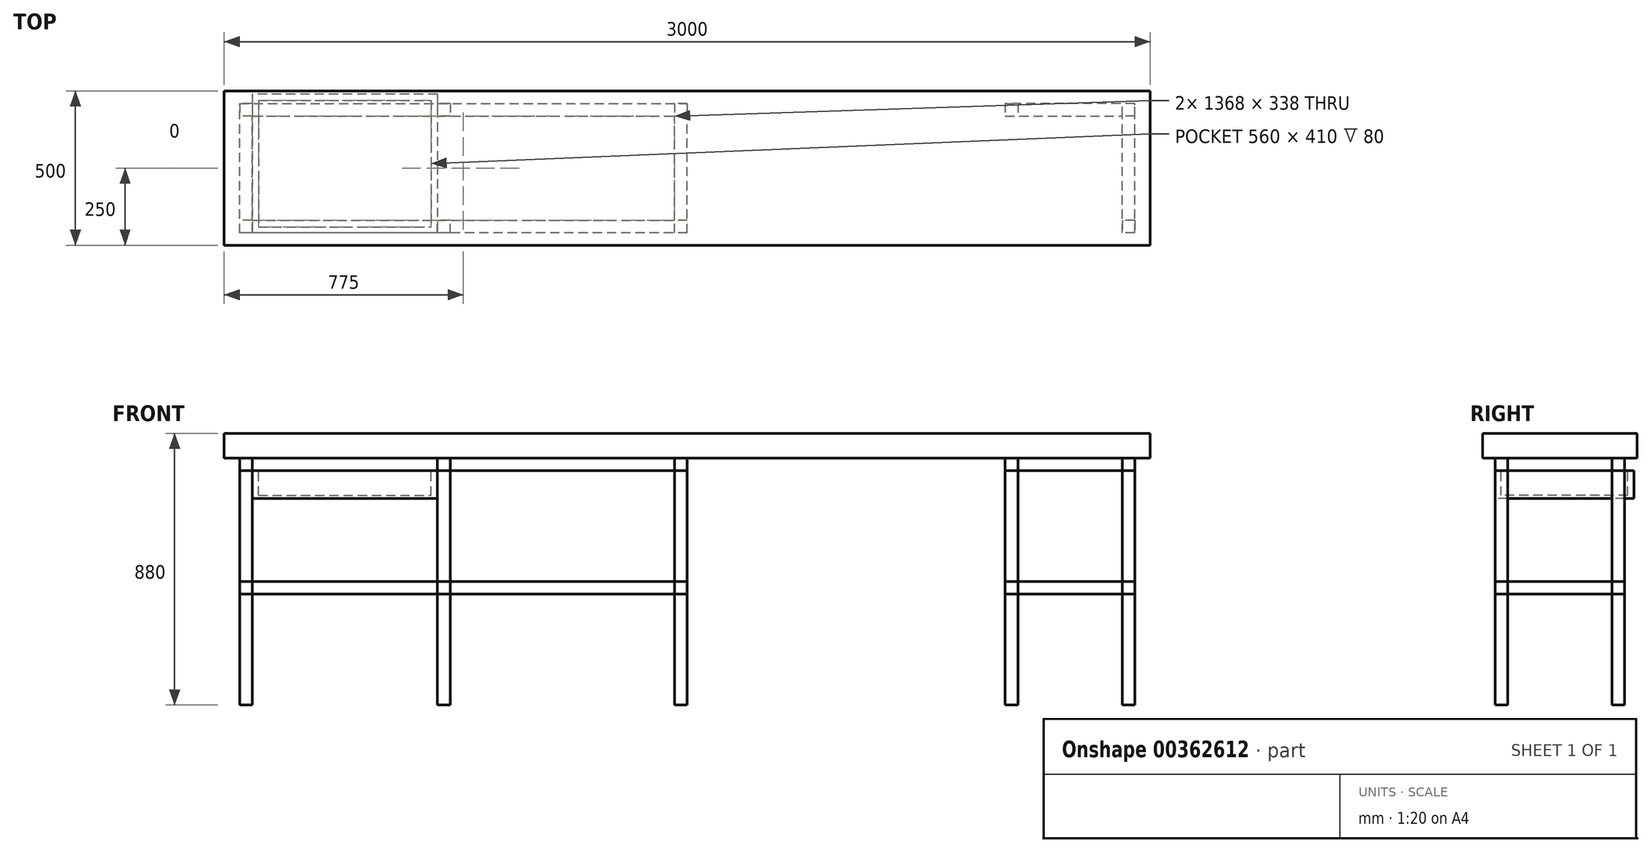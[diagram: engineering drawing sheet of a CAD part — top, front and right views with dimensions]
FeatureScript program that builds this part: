
annotation { "Feature Type Name" : "Feature", "Feature Type Description" : "" }
export const myFeature = defineFeature(function(context is Context, id is Id, definition is map)
    precondition{}
    {
        {
            var Q0;
            Q0=qCreatedBy(makeId("Top.planeOp"),FACE);
            var sketch = newSketch(context, id + "F0", { "sketchPlane" : qUnion([Q0])});
            skLineSegment(sketch, "E0.bottom", {"start": v(0, 0) * mm, "end": v(3000, 0) * mm});
            skLineSegment(sketch, "E0.top", {"start": v(0, 500) * mm, "end": v(3000, 500) * mm});
            skLineSegment(sketch, "E0.left", {"start": v(0, 0) * mm, "end": v(0, 500) * mm});
            skLineSegment(sketch, "E0.right", {"start": v(3000, 0) * mm, "end": v(3000, 500) * mm});
            skSolve(sketch);
        }
        {
            var Q0;
            Q0 = qSketchRegion(id + "F0", true);
            extrude(context, id + "F1", {"entities" : qUnion([Q0]), "depth" : 80 * mm});
        }
        {
            var Q0;
            Q0=makeQuery(id+"F1.opExtrude","CAP_FACE",FACE,{"disambiguationData":[OSD([sQuery(id+"F0.wireOp",EDGE,"E0.bottom"),sQuery(id+"F0.wireOp",EDGE,"E0.top"),sQuery(id+"F0.wireOp",EDGE,"E0.left"),sQuery(id+"F0.wireOp",EDGE,"E0.right")])],"isStart":true});
            var sketch = newSketch(context, id + "F2", { "sketchPlane" : qUnion([Q0])});
            skLineSegment(sketch, "E1.bottom", {"start": v(91, -40) * mm, "end": v(50, -40) * mm});
            skLineSegment(sketch, "E1.top", {"start": v(91, -81) * mm, "end": v(50, -81) * mm});
            skLineSegment(sketch, "E1.left", {"start": v(91, -40) * mm, "end": v(91, -81) * mm});
            skLineSegment(sketch, "E1.right", {"start": v(50, -40) * mm, "end": v(50, -81) * mm});
            skPoint(sketch, "E1.middle", {"position": v(70.5, -60.5) * mm});
            skLineSegment(sketch, "E2.bottom", {"start": v(3000, 0) * mm, "end": v(0, 0) * mm, "construction": true});
            skLineSegment(sketch, "E2.top", {"start": v(3000, -500) * mm, "end": v(0, -500) * mm, "construction": true});
            skLineSegment(sketch, "E2.left", {"start": v(3000, 0) * mm, "end": v(3000, -500) * mm, "construction": true});
            skLineSegment(sketch, "E2.right", {"start": v(0, 0) * mm, "end": v(0, -500) * mm, "construction": true});
            skPoint(sketch, "E2.middle", {"position": v(1500, -250) * mm});
            skLineSegment(sketch, "E3.bottom", {"start": v(2950, -40) * mm, "end": v(50, -40) * mm, "construction": true});
            skLineSegment(sketch, "E3.top", {"start": v(2950, -460) * mm, "end": v(50, -460) * mm, "construction": true});
            skLineSegment(sketch, "E3.left", {"start": v(2950, -40) * mm, "end": v(2950, -460) * mm, "construction": true});
            skLineSegment(sketch, "E3.right", {"start": v(50, -40) * mm, "end": v(50, -460) * mm, "construction": true});
            skLineSegment(sketch, "E4", {"start": v(50, -250) * mm, "end": v(0, -250) * mm, "construction": true});
            skLineSegment(sketch, "E5", {"start": v(1500, -460) * mm, "end": v(1500, -500) * mm, "construction": true});
            skLineSegment(sketch, "E6.bottom", {"start": v(91, -460) * mm, "end": v(50, -460) * mm});
            skLineSegment(sketch, "E6.top", {"start": v(91, -419) * mm, "end": v(50, -419) * mm});
            skLineSegment(sketch, "E6.left", {"start": v(91, -460) * mm, "end": v(91, -419) * mm});
            skLineSegment(sketch, "E6.right", {"start": v(50, -460) * mm, "end": v(50, -419) * mm});
            skPoint(sketch, "E6.middle", {"position": v(70.5, -439.5) * mm});
            skLineSegment(sketch, "E7.right", {"start": v(2812.92, 127.48) * mm, "end": v(2812.92, 114.66) * mm});
            skLineSegment(sketch, "E8.bottom", {"start": v(2950, -81) * mm, "end": v(2909, -81) * mm});
            skLineSegment(sketch, "E8.top", {"start": v(2950, -40) * mm, "end": v(2909, -40) * mm});
            skLineSegment(sketch, "E8.left", {"start": v(2950, -81) * mm, "end": v(2950, -40) * mm});
            skLineSegment(sketch, "E8.right", {"start": v(2909, -81) * mm, "end": v(2909, -40) * mm});
            skPoint(sketch, "E8.middle", {"position": v(2929.5, -60.5) * mm});
            skLineSegment(sketch, "E9.bottom", {"start": v(2950, -419) * mm, "end": v(2909, -419) * mm});
            skLineSegment(sketch, "E9.top", {"start": v(2950, -460) * mm, "end": v(2909, -460) * mm});
            skLineSegment(sketch, "E9.left", {"start": v(2950, -419) * mm, "end": v(2950, -460) * mm});
            skLineSegment(sketch, "E9.right", {"start": v(2909, -419) * mm, "end": v(2909, -460) * mm});
            skPoint(sketch, "E9.middle", {"position": v(2929.5, -439.5) * mm});
            skLineSegment(sketch, "E10.bottom", {"start": v(1500, -460) * mm, "end": v(1459, -460) * mm});
            skLineSegment(sketch, "E10.top", {"start": v(1500, -419) * mm, "end": v(1459, -419) * mm});
            skLineSegment(sketch, "E10.left", {"start": v(1500, -460) * mm, "end": v(1500, -419) * mm});
            skLineSegment(sketch, "E10.right", {"start": v(1459, -460) * mm, "end": v(1459, -419) * mm});
            skPoint(sketch, "E10.middle", {"position": v(1479.5, -439.5) * mm});
            skLineSegment(sketch, "E11", {"start": v(1500, 0) * mm, "end": v(1500, -40) * mm, "construction": true});
            skLineSegment(sketch, "E12.bottom", {"start": v(1500, -40) * mm, "end": v(1459, -40) * mm});
            skLineSegment(sketch, "E12.top", {"start": v(1500, -81) * mm, "end": v(1459, -81) * mm});
            skLineSegment(sketch, "E12.left", {"start": v(1500, -40) * mm, "end": v(1500, -81) * mm});
            skLineSegment(sketch, "E12.right", {"start": v(1459, -40) * mm, "end": v(1459, -81) * mm});
            skPoint(sketch, "E12.middle", {"position": v(1479.5, -60.5) * mm});
            skLineSegment(sketch, "E13", {"start": v(2909, -419) * mm, "end": v(2909, -81) * mm, "construction": true});
            skLineSegment(sketch, "E14", {"start": v(2909, -419) * mm, "end": v(2571, -419) * mm, "construction": true});
            skLineSegment(sketch, "E15.bottom", {"start": v(2530, -460) * mm, "end": v(2571, -460) * mm});
            skLineSegment(sketch, "E15.top", {"start": v(2530, -419) * mm, "end": v(2571, -419) * mm});
            skLineSegment(sketch, "E15.left", {"start": v(2530, -460) * mm, "end": v(2530, -419) * mm});
            skLineSegment(sketch, "E15.right", {"start": v(2571, -460) * mm, "end": v(2571, -419) * mm});
            skPoint(sketch, "E15.middle", {"position": v(2550.5, -439.5) * mm});
            skLineSegment(sketch, "E16", {"start": v(70.5, -60.5) * mm, "end": v(1479.5, -60.5) * mm, "construction": true});
            skLineSegment(sketch, "E17.bottom", {"start": v(732, -40) * mm, "end": v(691, -40) * mm});
            skLineSegment(sketch, "E17.top", {"start": v(732, -81) * mm, "end": v(691, -81) * mm});
            skLineSegment(sketch, "E17.left", {"start": v(732, -40) * mm, "end": v(732, -81) * mm});
            skLineSegment(sketch, "E17.right", {"start": v(691, -40) * mm, "end": v(691, -81) * mm});
            skPoint(sketch, "E17.middle", {"position": v(711.5, -60.5) * mm});
            skLineSegment(sketch, "E18", {"start": v(70.5, -439.5) * mm, "end": v(1479.5, -439.5) * mm, "construction": true});
            skLineSegment(sketch, "E19.bottom", {"start": v(732, -460) * mm, "end": v(691, -460) * mm});
            skLineSegment(sketch, "E19.top", {"start": v(732, -419) * mm, "end": v(691, -419) * mm});
            skLineSegment(sketch, "E19.left", {"start": v(732, -460) * mm, "end": v(732, -419) * mm});
            skLineSegment(sketch, "E19.right", {"start": v(691, -460) * mm, "end": v(691, -419) * mm});
            skPoint(sketch, "E19.middle", {"position": v(711.5, -439.5) * mm});
            skSolve(sketch);
        }
        {
            var Q0;
            Q0 = qSketchRegion(id + "F2", true);
            extrude(context, id + "F3", {"entities" : qUnion([Q0]), "depth" : 800 * mm});
        }
        {
            var Q0;
            Q0=makeQuery(id+"F3.opExtrude","CAP_FACE",FACE,{"disambiguationData":[OSD([sQuery(id+"F2.wireOp",EDGE,"E1.bottom"),sQuery(id+"F2.wireOp",EDGE,"E1.top"),sQuery(id+"F2.wireOp",EDGE,"E1.left"),sQuery(id+"F2.wireOp",EDGE,"E1.right")])],"isStart":true});
            var sketch = newSketch(context, id + "F4", { "sketchPlane" : qUnion([Q0])});
            skLineSegment(sketch, "E20.bottom", {"start": v(50, 40) * mm, "end": v(1500, 40) * mm});
            skLineSegment(sketch, "E20.top", {"start": v(50, 460) * mm, "end": v(1500, 460) * mm});
            skLineSegment(sketch, "E20.left", {"start": v(50, 40) * mm, "end": v(50, 460) * mm});
            skLineSegment(sketch, "E20.right", {"start": v(1500, 40) * mm, "end": v(1500, 460) * mm});
            skLineSegment(sketch, "E21.bottom", {"start": v(91, 81) * mm, "end": v(1459, 81) * mm});
            skLineSegment(sketch, "E21.top", {"start": v(91, 419) * mm, "end": v(1459, 419) * mm});
            skLineSegment(sketch, "E21.left", {"start": v(91, 81) * mm, "end": v(91, 419) * mm});
            skLineSegment(sketch, "E21.right", {"start": v(1459, 81) * mm, "end": v(1459, 419) * mm});
            skLineSegment(sketch, "E22.bottom", {"start": v(2950, 40) * mm, "end": v(2909, 40) * mm});
            skLineSegment(sketch, "E22.top", {"start": v(2950, 460) * mm, "end": v(2909, 460) * mm});
            skLineSegment(sketch, "E22.left", {"start": v(2950, 40) * mm, "end": v(2950, 460) * mm});
            skLineSegment(sketch, "E22.right", {"start": v(2909, 40) * mm, "end": v(2909, 419) * mm});
            skLineSegment(sketch, "E23.bottom", {"start": v(2530, 419) * mm, "end": v(2909, 419) * mm});
            skLineSegment(sketch, "E23.top", {"start": v(2530, 460) * mm, "end": v(2950, 460) * mm});
            skLineSegment(sketch, "E23.left", {"start": v(2530, 419) * mm, "end": v(2530, 460) * mm});
            skLineSegment(sketch, "E23.right", {"start": v(2950, 419) * mm, "end": v(2950, 460) * mm});
            skSolve(sketch);
        }
        {
            var Q0;
            Q0 = qSketchRegion(id + "F4", true);
            extrude(context, id + "F5", {"entities" : qUnion([Q0]), "oppositeDirection" : true, "depth" : 41 * mm});
        }
        {
            var Q0;
            Q0 = qSketchRegion(id + "F4", true);
            extrude(context, id + "F6", {"entities" : qUnion([Q0]), "oppositeDirection" : true, "depth" : 441 * mm, "hasSecondDirection" : true, "secondDirectionOppositeDirection" : true, "secondDirectionDepth" : 400 * mm});
        }
        {
            var Q0;
            Q0=makeQuery(id+"F5.opExtrude","SWEPT_FACE",FACE,{"disambiguationData":[OSD([sQuery(id+"F4.wireOp",EDGE,"E20.bottom")])]});
            var sketch = newSketch(context, id + "F7", { "sketchPlane" : qUnion([Q0])});
            skLineSegment(sketch, "E24", {"start": v(91, -41) * mm, "end": v(91, -400) * mm, "construction": true});
            skLineSegment(sketch, "E25", {"start": v(91, -220.5) * mm, "end": v(691, -220.5) * mm, "construction": true});
            skLineSegment(sketch, "E26", {"start": v(691, -220.5) * mm, "end": v(691, -41) * mm, "construction": true});
            skLineSegment(sketch, "E27", {"start": v(691, -130.75) * mm, "end": v(91, -130.75) * mm, "construction": true});
            skLineSegment(sketch, "E28", {"start": v(691, -220.5) * mm, "end": v(691, -400) * mm, "construction": true});
            skLineSegment(sketch, "E29", {"start": v(691, -310.25) * mm, "end": v(91, -310.25) * mm, "construction": true});
            skLineSegment(sketch, "E30.bottom", {"start": v(91, -41) * mm, "end": v(691, -41) * mm});
            skLineSegment(sketch, "E30.top", {"start": v(91, -130.75) * mm, "end": v(691, -130.75) * mm});
            skLineSegment(sketch, "E30.left", {"start": v(91, -41) * mm, "end": v(91, -130.75) * mm});
            skLineSegment(sketch, "E30.right", {"start": v(691, -41) * mm, "end": v(691, -130.75) * mm});
            skSolve(sketch);
        }
        {
            var Q0;
            Q0=makeQuery(id+"F7.imprint","IMPRINT",FACE,{"disambiguationData":[TD([[makeQuery(id+"F7.imprint","IMPRINT",EDGE,{"derivedFrom":sQuery(id+"F7.wireOp",EDGE,"E30.bottom")}),1.0]])]});
            extrude(context, id + "F8", {"entities" : qUnion([Q0]), "oppositeDirection" : true, "depth" : 450 * mm});
        }
        {
            var Q0;
            Q0=makeQuery(id+"F8.opExtrude","SWEPT_FACE",FACE,{"disambiguationData":[OSD([sQuery(id+"F7.wireOp",EDGE,"E30.bottom")])]});
            var sketch = newSketch(context, id + "F9", { "sketchPlane" : qUnion([Q0])});
            skLineSegment(sketch, "E31.bottom", {"start": v(91, 490) * mm, "end": v(691, 490) * mm, "construction": true});
            skLineSegment(sketch, "E31.top", {"start": v(91, 40) * mm, "end": v(691, 40) * mm, "construction": true});
            skLineSegment(sketch, "E31.left", {"start": v(91, 490) * mm, "end": v(91, 40) * mm, "construction": true});
            skLineSegment(sketch, "E31.right", {"start": v(691, 490) * mm, "end": v(691, 40) * mm, "construction": true});
            skLineSegment(sketch, "E32.bottom", {"start": v(91, 490) * mm, "end": v(111, 490) * mm, "construction": true});
            skLineSegment(sketch, "E32.top", {"start": v(91, 470) * mm, "end": v(111, 470) * mm, "construction": true});
            skLineSegment(sketch, "E32.left", {"start": v(91, 490) * mm, "end": v(91, 470) * mm, "construction": true});
            skLineSegment(sketch, "E32.right", {"start": v(111, 490) * mm, "end": v(111, 470) * mm, "construction": true});
            skLineSegment(sketch, "E33.bottom", {"start": v(691, 40) * mm, "end": v(671, 40) * mm, "construction": true});
            skLineSegment(sketch, "E33.top", {"start": v(691, 60) * mm, "end": v(671, 60) * mm, "construction": true});
            skLineSegment(sketch, "E33.left", {"start": v(691, 40) * mm, "end": v(691, 60) * mm, "construction": true});
            skLineSegment(sketch, "E33.right", {"start": v(671, 40) * mm, "end": v(671, 60) * mm, "construction": true});
            skLineSegment(sketch, "E34.bottom", {"start": v(111, 470) * mm, "end": v(671, 470) * mm});
            skLineSegment(sketch, "E34.top", {"start": v(111, 60) * mm, "end": v(671, 60) * mm});
            skLineSegment(sketch, "E34.left", {"start": v(111, 470) * mm, "end": v(111, 60) * mm});
            skLineSegment(sketch, "E34.right", {"start": v(671, 470) * mm, "end": v(671, 60) * mm});
            skSolve(sketch);
        }
        {
            var Q0;
            Q0=makeQuery(id+"F9.imprint","IMPRINT",FACE,{"disambiguationData":[TD([[makeQuery(id+"F9.imprint","IMPRINT",EDGE,{"derivedFrom":sQuery(id+"F9.wireOp",EDGE,"E34.bottom")}),-1.0]])]});
            extrude(context, id + "F10", {"entities" : qUnion([Q0]), "operationType" : NewBodyOperationType.REMOVE, "oppositeDirection" : true, "depth" : 80 * mm});
        }
    });
